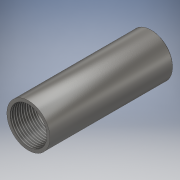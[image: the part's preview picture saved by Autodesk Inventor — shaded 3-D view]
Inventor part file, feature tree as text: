
AUTODESK INVENTOR PART (.ipt)
format: ipt  version: 2019 (Build 230136000, 136)  size: 117,248 bytes
history: native  units: mm
features: extrude x1, other x1, chamfer x1, sketch x1
ambient origin geometry x8: Origin, YZ Plane, XZ Plane, XY Plane, X Axis, Y Axis, Z Axis, Center Point
bodies: Solide1 (feature_tree)
feature tree (4):
  extrude  "Extrusion1"  Depth=2.5mm
  other  "Filetage1"
  chamfer  "Chanfrein1"  Distance=35.0mm
  sketch  "Esquisse1"
